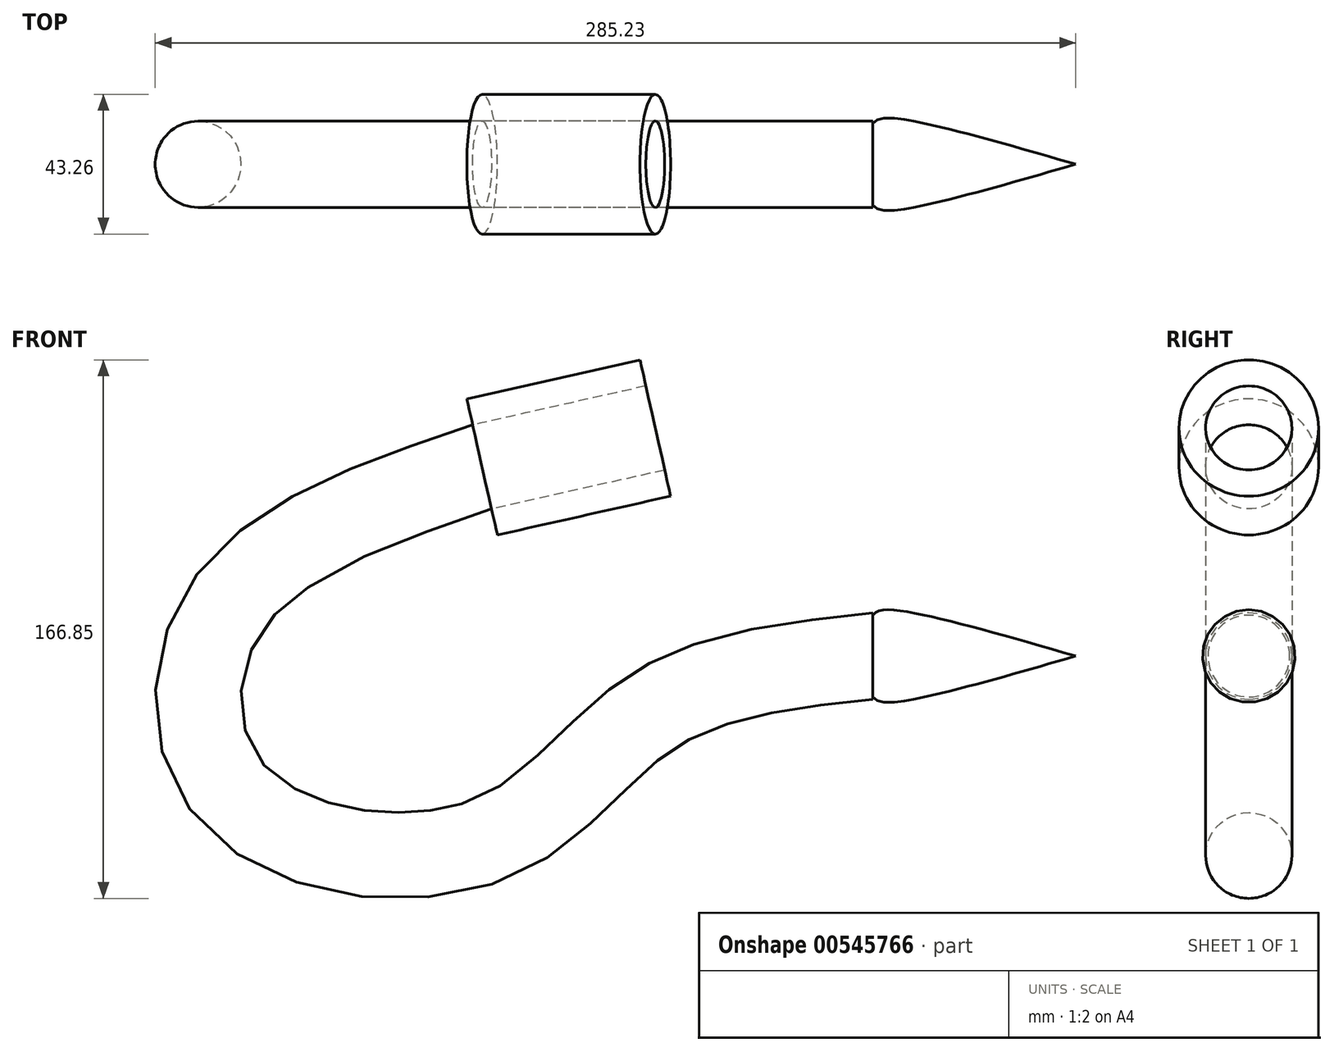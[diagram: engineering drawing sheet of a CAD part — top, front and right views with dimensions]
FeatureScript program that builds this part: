
annotation { "Feature Type Name" : "Feature", "Feature Type Description" : "" }
export const myFeature = defineFeature(function(context is Context, id is Id, definition is map)
    precondition{}
    {
        {
            var Q0;
            Q0=qCreatedBy(makeId("Right.planeOp"),FACE);
            var sketch = newSketch(context, id + "F0", { "sketchPlane" : qUnion([Q0])});
            skCircle(sketch, "E0", {"center": v(0, 0) * mm, "radius": 13.36 * mm});
            skSolve(sketch);
        }
        {
            var Q0;
            Q0=qCreatedBy(makeId("Front.planeOp"),FACE);
            var sketch = newSketch(context, id + "F1", { "sketchPlane" : qUnion([Q0])});
            skFitSpline(sketch, "E1", {"points": [v(0, 0) * mm, v(-68.39, -17.17) * mm, v(-119.6, -57.14) * mm, v(-197.47, -43.82) * mm, v(-201.02, 14.21) * mm, v(-121.09, 58.62) * mm], "startDerivative": vector(-379.62, -39.74) * mm, "endDerivative": vector(437.66, 147.5) * mm});
            skSolve(sketch);
        }
        {
            var Q0;
            Q0=makeQuery(id+"F0.imprint","IMPRINT",FACE,{"disambiguationData":[TD([[makeQuery(id+"F0.imprint","IMPRINT",EDGE,{"derivedFrom":sQuery(id+"F0.wireOp",EDGE,"E0")}),1.0]])]});
            var Q1;
            Q1=sQuery(id+"F1.wireOp",EDGE,"E1");
            sweep(context, id + "F2", {"profiles" : qUnion([Q0]), "path" : qUnion([Q1])});
        }
        {
            var Q0;
            Q0=makeQuery(id+"F2.opSweep","CAP_FACE",FACE,{"disambiguationData":[OSD([sQuery(id+"F0.wireOp",EDGE,"E0"),sQuery(id+"F1.wireOp",VERTEX,"E1.end")])],"isStart":false});
            var sketch = newSketch(context, id + "F3", { "sketchPlane" : qUnion([Q0])});
            skCircle(sketch, "E2", {"center": v(0, 83.71) * mm, "radius": 21.63 * mm});
            skSolve(sketch);
        }
        {
            var Q0;
            Q0=makeQuery(id+"F3.imprint","IMPRINT",FACE,{"disambiguationData":[TD([[makeQuery(id+"F3.imprint","IMPRINT",EDGE,{"derivedFrom":sQuery(id+"F3.wireOp",EDGE,"E2")}),1.0]])]});
            extrude(context, id + "F4", {"entities" : qUnion([Q0]), "depth" : 55 * mm, "offsetDistance" : 25 * mm});
        }
        {
            var Q0;
            Q0=qCreatedBy(makeId("Front.planeOp"),FACE);
            var sketch = newSketch(context, id + "F5", { "sketchPlane" : qUnion([Q0])});
            skLineSegment(sketch, "E3", {"start": v(0, 0) * mm, "end": v(62.84, 0) * mm});
            skFitSpline(sketch, "E4", {"points": [v(62.84, 0) * mm, v(11.02, 13.66) * mm, v(0, 12.66) * mm, v(0, 0) * mm], "startDerivative": vector(-115.6, 33.5) * mm, "endDerivative": vector(10.4, -61.7) * mm});
            skSolve(sketch);
        }
        {
            var Q0;
            Q0=makeQuery(id+"F5.imprint","IMPRINT",FACE,{"disambiguationData":[TD([[makeQuery(id+"F5.imprint","IMPRINT",EDGE,{"derivedFrom":sQuery(id+"F5.wireOp",EDGE,"E3")}),1.0]])]});
            var Q1;
            Q1=sQuery(id+"F5.wireOp",EDGE,"E3");
            revolve(context, id + "F6", {"operationType" : NewBodyOperationType.ADD, "entities" : qUnion([Q0]), "axis" : qUnion([Q1]), "revolveType" : RevolveType.FULL});
        }
    });
